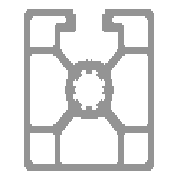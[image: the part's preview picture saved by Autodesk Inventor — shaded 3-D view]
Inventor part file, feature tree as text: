
AUTODESK INVENTOR PART (.ipt)
format: ipt  version: 2016 SP1 (Build 200210100, 210)  size: 437,760 bytes
history: native  units: mm
features: sketch x11, other x8, extrude x6, hole x2, plane x1
ambient origin geometry x8: Origin, YZ Plane, XZ Plane, XY Plane, X Axis, Y Axis, Z Axis, Center Point
bodies: Solid1 (feature_tree), Body (feature_tree)
feature tree (28):
  other  "45x45 1S"
  other  "Table"
  other  "Driven Length"
  other  "45x45 1S-01"
  other  "Blocks"
  other  "Start Plane"
  other  "End Plane"
  hole  "M12/-"  [1 undecoded]
  hole  "-/M12"  [1 undecoded]
  extrude  "D17/-"  Depth=10.0mm TaperAngle=0.0deg
  extrude  "-/D17"  Depth=22.5mm
  extrude  "D9.8/-"  Depth=10.0mm
  extrude  "-/D9.8"  Depth=10.0mm TaperAngle=0.0deg
  extrude  "-/D9.8VS"  Depth=22.5mm
  extrude  "D9.8VS/-"  Depth=10.0mm
  sketch  "Sketch1"  dims[d2=-0.0mm d3=1000.0mm]
  sketch  "Sketch9"  dims[d4=0.13mm d5=0.0mm]
  sketch  "Sketch10"  dims[d17=10.106mm d18=6.0mm d19=4.0mm d20=2.0mm d21=90.0deg d22=55.0mm d23=20.594885mm]
  sketch  "Sketch11"  dims[d24=10.106mm d25=6.0mm d26=4.0mm d27=2.0mm d28=90.0deg d29=55.0mm d30=20.594885mm d31=22.5mm]
  sketch  "Sketch12"  dims[d32=17.0mm d33=10.0mm d34=0.0mm]
  sketch  "Sketch13"  dims[d35=17.0mm d36=22.5mm]
  sketch  "Sketch14"  dims[d37=10.0mm d38=0.0mm d39=9.8mm]
  sketch  "Sketch15"  dims[d40=22.5mm d41=10.0mm d42=0.0mm]
  sketch  "Sketch26"  dims[d43=9.8mm d44=22.5mm]
  sketch  "Sketch47"  dims[d45=10.0mm d46=0.0mm d47=9.8mm]
  plane  "Work Plane21"
  sketch  "Sketch48"  dims[d48=22.5mm d49=10.0mm d50=0.0mm d62=9.8mm d63=10.0mm d64=0.0mm d65=22.5mm d86=90.0deg d7=1000.0mm]
  other  "45x45 1S:1"
note: 2 required parameter values undecoded (feature->parameter linkage not recoverable at this tier; creation-order binding heuristic only, values carry confidence <= 0.55)
